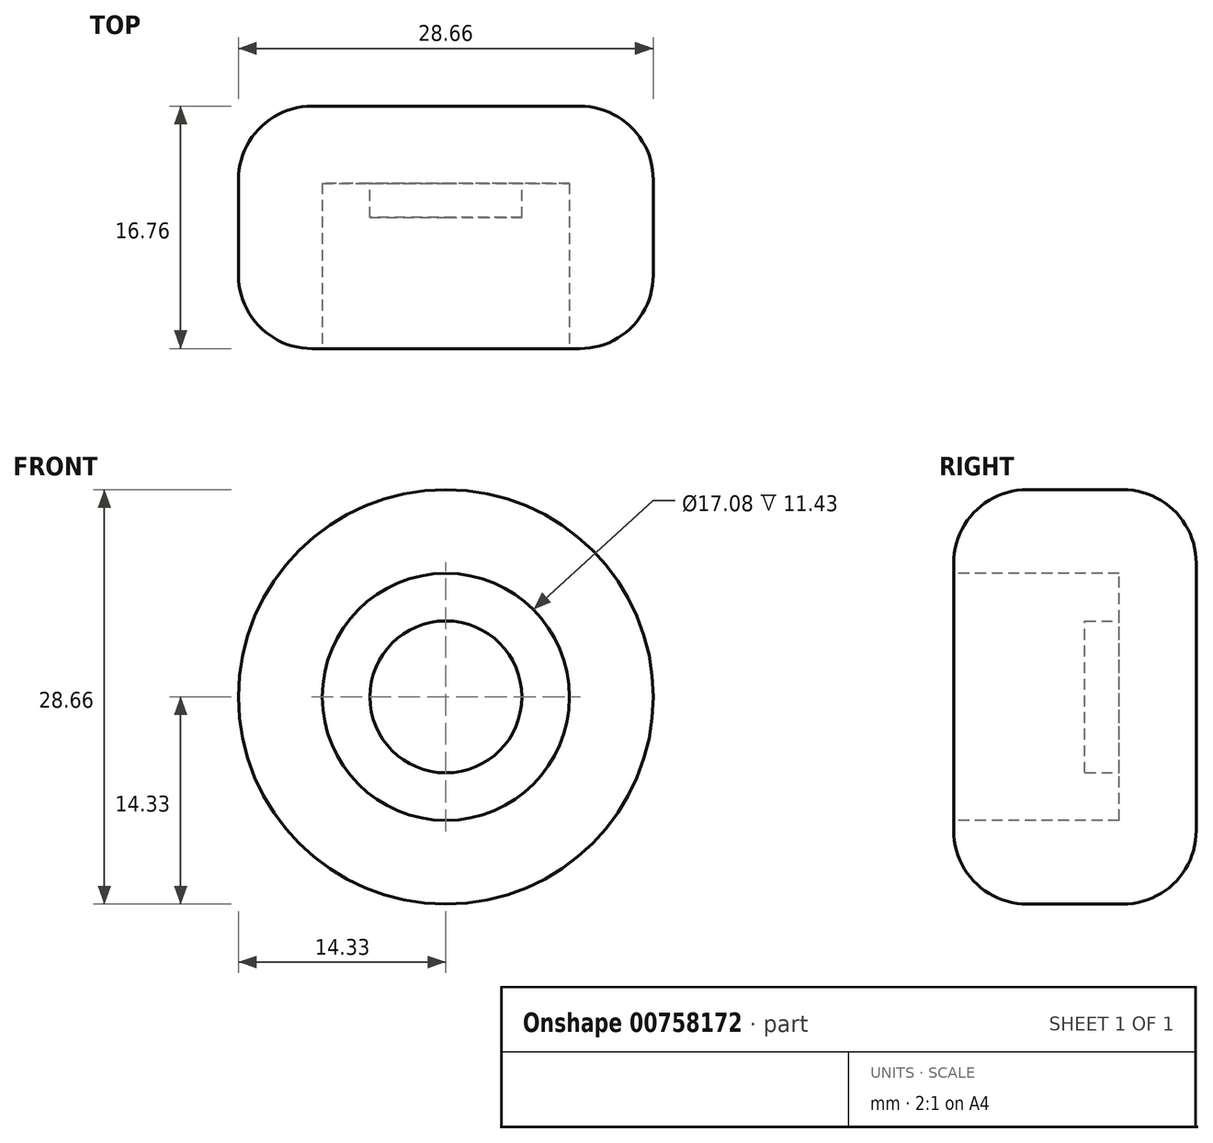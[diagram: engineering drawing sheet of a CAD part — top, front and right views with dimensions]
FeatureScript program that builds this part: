
annotation { "Feature Type Name" : "Feature", "Feature Type Description" : "" }
export const myFeature = defineFeature(function(context is Context, id is Id, definition is map)
    precondition{}
    {
        {
            var Q0;
            Q0=qCreatedBy(makeId("Front.planeOp"),FACE);
            var sketch = newSketch(context, id + "F0", { "sketchPlane" : qUnion([Q0])});
            skCircle(sketch, "E0", {"center": v(0, 0) * mm, "radius": 14.33 * mm});
            skSolve(sketch);
        }
        {
            var Q0;
            Q0=makeQuery(id+"F0.imprint","IMPRINT",FACE,{"disambiguationData":[TD([[makeQuery(id+"F0.imprint","IMPRINT",EDGE,{"derivedFrom":sQuery(id+"F0.wireOp",EDGE,"E0")}),1.0]])]});
            extrude(context, id + "F1", {"entities" : qUnion([Q0]), "depth" : 16.76 * mm, "offsetDistance" : 25.4 * mm});
        }
        {
            var Q0;
            Q0=makeQuery(id+"F1.opExtrude","CAP_EDGE",EDGE,{"disambiguationData":[OSD([sQuery(id+"F0.wireOp",EDGE,"E0")])],"isStart":false});
            fillet(context, id + "F2", {"entities" : qUnion([Q0]), "radius" : 5.08 * mm, "tangentPropagation" : true, "allowEdgeOverflow" : false});
        }
        {
            var Q0;
            Q0=makeQuery(id+"F1.opExtrude","CAP_EDGE",EDGE,{"disambiguationData":[OSD([sQuery(id+"F0.wireOp",EDGE,"E0")])],"isStart":true});
            fillet(context, id + "F3", {"entities" : qUnion([Q0]), "radius" : 5.08 * mm, "tangentPropagation" : true, "allowEdgeOverflow" : false});
        }
        {
            var Q0;
            Q0=makeQuery(id+"F1.opExtrude","CAP_FACE",FACE,{"disambiguationData":[OSD([sQuery(id+"F0.wireOp",EDGE,"E0")])],"isStart":false});
            var sketch = newSketch(context, id + "F4", { "sketchPlane" : qUnion([Q0])});
            skCircle(sketch, "E1", {"center": v(0, 0) * mm, "radius": 8.54 * mm});
            skSolve(sketch);
        }
        {
            var Q0;
            Q0 = qSketchRegion(id + "F4", true);
            extrude(context, id + "F5", {"entities" : qUnion([Q0]), "operationType" : NewBodyOperationType.REMOVE, "oppositeDirection" : true, "depth" : 11.43 * mm, "offsetDistance" : 25.4 * mm});
        }
        {
            var Q0;
            Q0=makeQuery(id+"F5.boolean.opBoolean","COPY",FACE,{"derivedFrom":makeQuery(id+"F5.opExtrude","CAP_FACE",FACE,{"disambiguationData":[OSD([sQuery(id+"F4.wireOp",EDGE,"E1")])],"isStart":false})});
            var sketch = newSketch(context, id + "F6", { "sketchPlane" : qUnion([Q0])});
            skCircle(sketch, "E2", {"center": v(0, 0) * mm, "radius": 5.25 * mm});
            skSolve(sketch);
        }
        {
            var Q0;
            Q0 = qSketchRegion(id + "F6", true);
            extrude(context, id + "F7", {"entities" : qUnion([Q0]), "operationType" : NewBodyOperationType.ADD, "depth" : 2.36 * mm, "offsetDistance" : 25.4 * mm});
        }
    });
